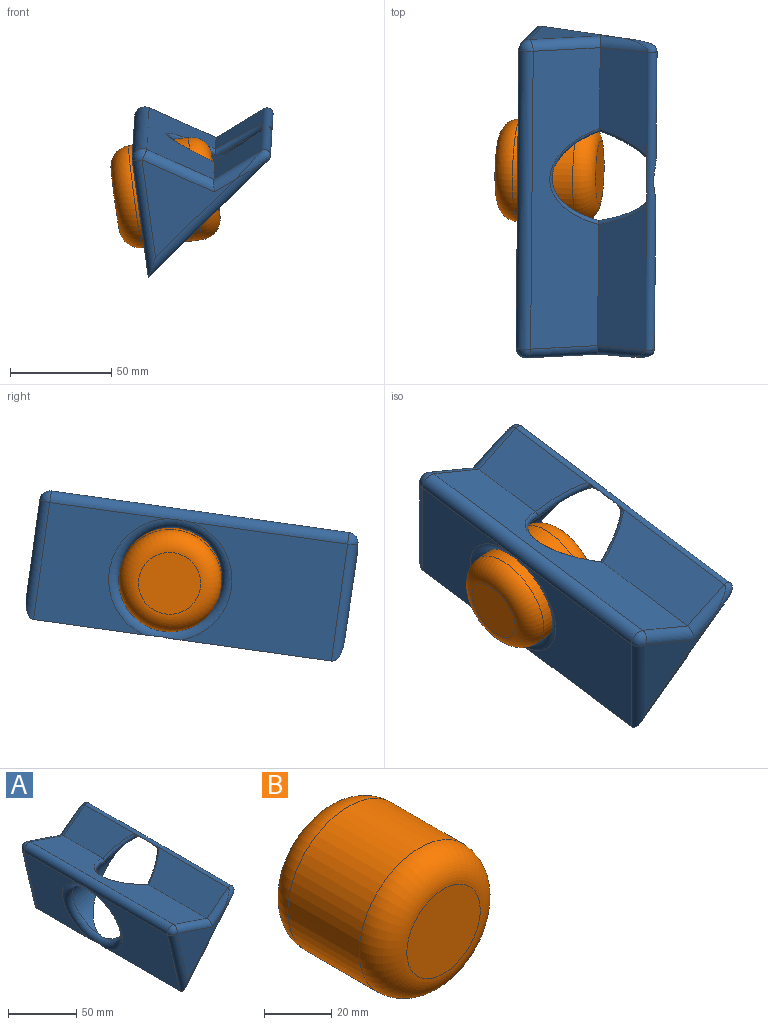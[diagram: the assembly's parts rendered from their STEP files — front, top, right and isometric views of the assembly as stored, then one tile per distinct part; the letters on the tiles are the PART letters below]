
ASSEMBLY  parts=2 mates=1
PART A: 30 faces, bbox 84.6x179.7x91.3 mm
  f0: bspline ~22.95x3.75mm, area 53mm2, adj f1,f14,f15,f28
  f1: bspline ~5.33x4.9mm, area 5.5mm2, adj f0,f14,f15,f26
  f2: plane 51.46x22.05mm, normal (-0.6,0,0.8), area 1233.3mm2, adj f6,f15,f20,f26
  f3: plane 78.09x57.3mm, normal (-0.97,0,-0.23), area 3514.3mm2, adj f8,f13,f17,f18
  f4: plane 47.68x47.12mm, normal (0,-1,0), area 892.3mm2, adj f10,f11,f12,f13,f19
  f5: plane 71.55x22.05mm, normal (-0.6,0,0.8), area 1787.6mm2, adj f6,f10,f15,f29
  f6: plane 148.5x34.32mm, normal (0.32,0,0.95), area 4471.9mm2, adj f2,f5,f12,f18,f22,f26,f27,f29
  f7: plane 58x57.3mm, normal (-0.97,0,-0.23), area 2331.7mm2, adj f8,f17,f18,f25
  f8: plane 148.5x63.92mm, normal (0.77,0,-0.64), area 9143.5mm2, adj f3,f7,f11,f14,f15,f17,f23
  f9: plane 47.43x46.53mm, normal (0,1,0), area 879.8mm2, adj f20,f22,f23,f25
  f10: cylinder r=5mm len=27.16mm, axis (0.8,0,0.6), area 158.5mm2, adj f4,f5,f12,f16
  f11: cylinder r=5mm len=67.13mm, axis (-0.64,0,-0.77), area 547.2mm2, adj f4,f8,f13,f16
  f12: cylinder r=5mm len=38.43mm, axis (0.95,0,-0.32), area 295mm2, adj f4,f6,f10,f19
  f13: cylinder r=5mm len=58.45mm, axis (-0.23,0,0.97), area 423.1mm2, adj f3,f4,f11,f19
  f14: cylinder r=25.4mm len=72.82mm, axis (-0.97,0,-0.23), area 3327.1mm2, adj f0,f1,f8,f15,f17,f26,f27,f28
  f15: cylinder r=3mm len=148.5mm, axis (0,1,0), area 1198.6mm2, adj f0,f1,f2,f5,f8,f14,f16,f21
  f16: bspline ~31.89x31.24mm, area 58.1mm2, adj f10,f11,f15
  f17: torus R=30.48mm, axis (-0.97,0,-0.23), area 1342mm2, adj f3,f7,f8,f14,f18
  f18: cylinder r=5.08mm len=148.5mm, axis (0,1,0), area 1603mm2, adj f3,f6,f7,f17,f19,f24
  f19: torus R=0.08mm, axis (0,-1,0), area 54.5mm2, adj f4,f12,f13,f18
  f20: cylinder r=5.08mm len=27.25mm, axis (-0.8,0,-0.6), area 158.4mm2, adj f2,f9,f21,f22
  f21: bspline ~32.4x30.75mm, area 59.5mm2, adj f15,f20,f23
  f22: cylinder r=5.08mm len=38.49mm, axis (-0.95,0,0.32), area 299.9mm2, adj f6,f9,f20,f24
  f23: cylinder r=5.08mm len=67.18mm, axis (0.64,0,0.77), area 552.5mm2, adj f8,f9,f21,f25
  f24: sphere r=5.08mm, area 38mm2, adj f18,f22,f25
  f25: cylinder r=5.08mm len=58.46mm, axis (0.23,0,-0.97), area 429.2mm2, adj f7,f9,f23,f24
  f26: bspline ~24.55x19.73mm, area 133.8mm2, adj f1,f2,f6,f14,f27
  f27: bspline ~48.54x26.63mm, area 339.9mm2, adj f6,f14,f26,f29
  f28: bspline ~3.32x2.63mm, area 5.6mm2, adj f0,f14,f15,f29
  f29: bspline ~24.55x19.73mm, area 133.7mm2, adj f5,f6,f14,f27,f28
PART B: 5 faces, bbox 55x50x55 mm
  f0: cylinder r=25.4mm len=50.8mm, axis (0,1,0), area 4787.8mm2, adj f3,f4
  f1: plane 30.8x30.8mm, normal (0,-1,0), area 745.1mm2, adj f4
  f2: plane 30.8x30.8mm, normal (0,1,0), area 745.1mm2, adj f3
  f3: torus R=15.4mm, axis (0,-1,0), area 2148.2mm2, adj f0,f2
  f4: torus R=15.4mm, axis (0,-1,0), area 2148.2mm2, adj f0,f1
PLACE A rot(axis=(0.82,0.57,-0.01),9.7deg) t=(50.59,14.9,74.23)mm fixed
PLACE B rot(axis=(0.13,0,-0.99),91.6deg) t=(51.35,-51.73,50.36)mm
MATE slider B.f0 <-> A.f14  axis (0.99,-0.03,0.13) through (26.58,-51.05,47.04)mm
